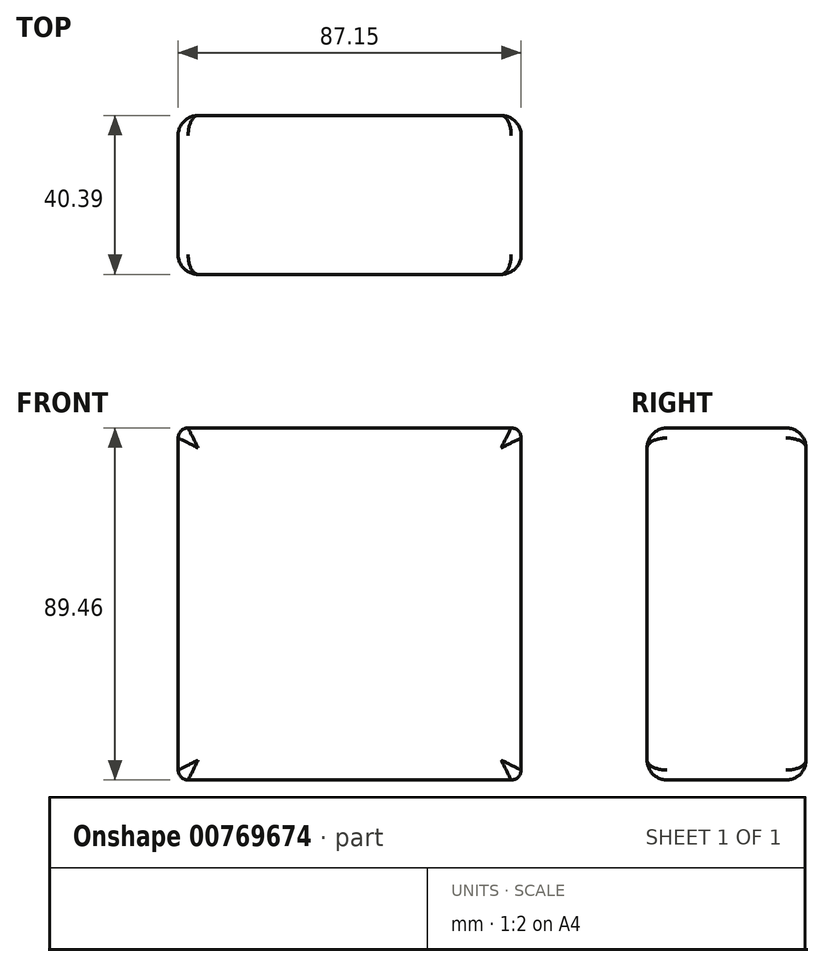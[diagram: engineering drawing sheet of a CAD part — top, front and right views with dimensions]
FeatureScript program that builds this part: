
annotation { "Feature Type Name" : "Feature", "Feature Type Description" : "" }
export const myFeature = defineFeature(function(context is Context, id is Id, definition is map)
    precondition{}
    {
        {
            var Q0;
            Q0=qCreatedBy(makeId("Front.planeOp"),FACE);
            var sketch = newSketch(context, id + "F0", { "sketchPlane" : qUnion([Q0])});
            skLineSegment(sketch, "E0.bottom", {"start": v(-40.3, 46.17) * mm, "end": v(46.86, 46.17) * mm});
            skLineSegment(sketch, "E0.top", {"start": v(-40.3, -43.3) * mm, "end": v(46.86, -43.3) * mm});
            skLineSegment(sketch, "E0.left", {"start": v(-40.3, 46.17) * mm, "end": v(-40.3, -43.3) * mm});
            skLineSegment(sketch, "E0.right", {"start": v(46.86, 46.17) * mm, "end": v(46.86, -43.3) * mm});
            skSolve(sketch);
        }
        {
            var Q0;
            Q0=makeQuery(id+"F0.imprint","IMPRINT",FACE,{"disambiguationData":[TD([[makeQuery(id+"F0.imprint","IMPRINT",EDGE,{"derivedFrom":sQuery(id+"F0.wireOp",EDGE,"E0.bottom")}),-1.0]])]});
            extrude(context, id + "F1", {"entities" : qUnion([Q0]), "oppositeDirection" : true, "depth" : 40.4 * mm, "offsetDistance" : 25.4 * mm});
        }
        {
            var Q0;
            Q0=makeQuery(id+"F1.opExtrude","SWEPT_EDGE",EDGE,{"disambiguationData":[OSD([sQuery(id+"F0.wireOp",EDGE,"E0.bottom"),sQuery(id+"F0.wireOp",EDGE,"E0.left")])]});
            var Q1;
            Q1=makeQuery(id+"F1.opExtrude","SWEPT_EDGE",EDGE,{"disambiguationData":[OSD([sQuery(id+"F0.wireOp",EDGE,"E0.bottom"),sQuery(id+"F0.wireOp",EDGE,"E0.right")])]});
            var Q2;
            Q2=makeQuery(id+"F1.opExtrude","SWEPT_EDGE",EDGE,{"disambiguationData":[OSD([sQuery(id+"F0.wireOp",EDGE,"E0.top"),sQuery(id+"F0.wireOp",EDGE,"E0.left")])]});
            var Q3;
            Q3=makeQuery(id+"F1.opExtrude","SWEPT_EDGE",EDGE,{"disambiguationData":[OSD([sQuery(id+"F0.wireOp",EDGE,"E0.top"),sQuery(id+"F0.wireOp",EDGE,"E0.right")])]});
            fillet(context, id + "F2", {"entities" : qUnion([Q0, Q1, Q2, Q3]), "radius" : 2.54 * mm, "tangentPropagation" : true, "allowEdgeOverflow" : false});
        }
        {
            var Q0;
            Q0=makeQuery(id+"F1.opExtrude","CAP_EDGE",EDGE,{"disambiguationData":[OSD([sQuery(id+"F0.wireOp",EDGE,"E0.bottom")])],"isStart":true});
            var Q1;
            Q1=makeQuery(id+"F1.opExtrude","CAP_EDGE",EDGE,{"disambiguationData":[OSD([sQuery(id+"F0.wireOp",EDGE,"E0.bottom")])],"isStart":false});
            fillet(context, id + "F3", {"entities" : qUnion([Q0, Q1]), "radius" : 5.08 * mm, "tangentPropagation" : true, "allowEdgeOverflow" : false});
        }
        {
            var Q0;
            Q0=makeQuery(id+"F1.opExtrude","SWEPT_FACE",FACE,{"disambiguationData":[OSD([sQuery(id+"F0.wireOp",EDGE,"E0.right")])]});
            var sketch = newSketch(context, id + "F4", { "sketchPlane" : qUnion([Q0])});
            skCircle(sketch, "E1", {"center": v(18.87, 28.28) * mm, "radius": 2.11 * mm});
            skCircle(sketch, "E2", {"center": v(18.74, 21.37) * mm, "radius": 2.37 * mm});
            skSolve(sketch);
        }
        {
            var Q0;
            Q0=makeQuery(id+"F4.imprint","IMPRINT",FACE,{"disambiguationData":[TD([[makeQuery(id+"F4.imprint","IMPRINT",EDGE,{"derivedFrom":sQuery(id+"F4.wireOp",EDGE,"E1")}),1.0]])]});
            extrude(context, id + "F5", {"entities" : qUnion([Q0]), "operationType" : NewBodyOperationType.ADD, "oppositeDirection" : true, "depth" : 2.03 * mm, "offsetDistance" : 25.4 * mm});
        }
        {
            var Q0;
            Q0=makeQuery(id+"F4.imprint","IMPRINT",FACE,{"disambiguationData":[TD([[makeQuery(id+"F4.imprint","IMPRINT",EDGE,{"derivedFrom":sQuery(id+"F4.wireOp",EDGE,"E2")}),1.0]])]});
            extrude(context, id + "F6", {"entities" : qUnion([Q0]), "operationType" : NewBodyOperationType.ADD, "oppositeDirection" : true, "depth" : 3.05 * mm, "offsetDistance" : 25.4 * mm});
        }
    });
